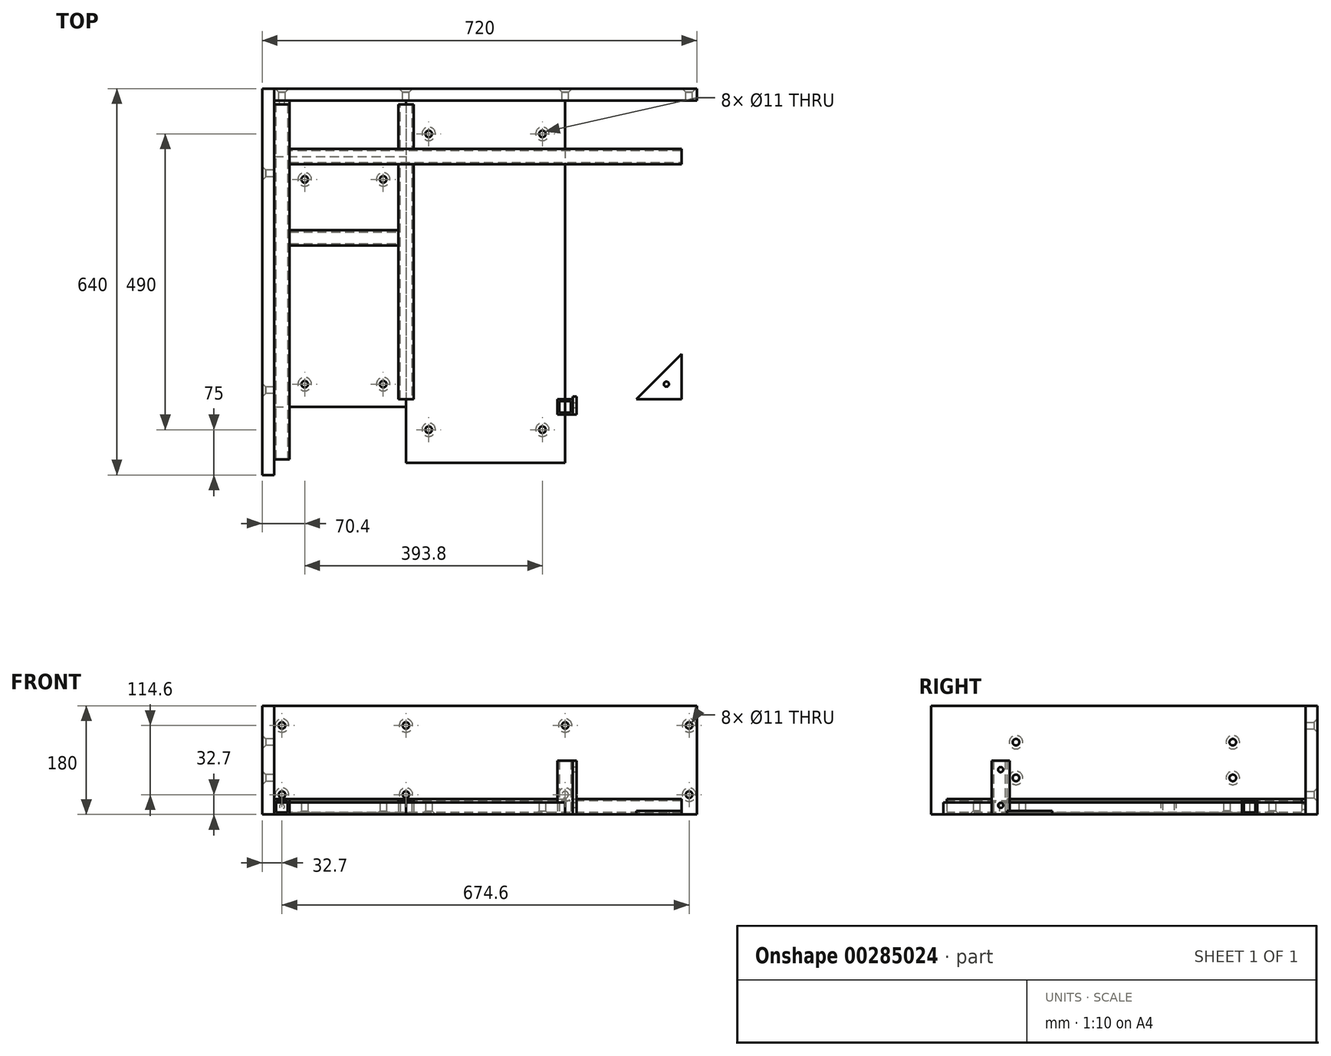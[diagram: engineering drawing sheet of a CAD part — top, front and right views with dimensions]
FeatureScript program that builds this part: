
annotation { "Feature Type Name" : "Feature", "Feature Type Description" : "" }
export const myFeature = defineFeature(function(context is Context, id is Id, definition is map)
    precondition{}
    {
        {
            assignVariable(context, id + "F0", {"name" : "plate", "anyValue" : 6});
        }
        {
            var Q0;
            Q0=qCreatedBy(makeId("Top.planeOp"),FACE);
            var sketch = newSketch(context, id + "F1", { "sketchPlane" : qUnion([Q0])});
            skLineSegment(sketch, "E0.bottom", {"start": v(350, -300) * mm, "end": v(-350, -300) * mm});
            skLineSegment(sketch, "E0.top", {"start": v(350, 300) * mm, "end": v(-350, 300) * mm});
            skLineSegment(sketch, "E0.left", {"start": v(350, -300) * mm, "end": v(350, 300) * mm});
            skLineSegment(sketch, "E0.right", {"start": v(-350, -300) * mm, "end": v(-350, 300) * mm});
            skPoint(sketch, "E0.middle", {"position": v(0, 0) * mm});
            skLineSegment(sketch, "E1", {"start": v(-324.6, 300) * mm, "end": v(-324.6, -300) * mm});
            skLineSegment(sketch, "E2", {"start": v(324.6, 300) * mm, "end": v(324.6, -300) * mm});
            skLineSegment(sketch, "E3", {"start": v(324.6, 220) * mm, "end": v(-324.6, 220) * mm});
            skLineSegment(sketch, "E4", {"start": v(-324.6, 194.6) * mm, "end": v(324.6, 194.6) * mm});
            skLineSegment(sketch, "E5", {"start": v(-119.2, 300) * mm, "end": v(-119.2, 220) * mm});
            skPoint(sketch, "E5.endSnap0", {"position": v(0, 220) * mm});
            skLineSegment(sketch, "E6", {"start": v(-144.6, 220) * mm, "end": v(-144.6, 300) * mm});
            skLineSegment(sketch, "E7.MirrorCS", {"start": v(119.2, 300) * mm, "end": v(119.2, 220) * mm});
            skLineSegment(sketch, "E8.MirrorCS", {"start": v(144.6, 220) * mm, "end": v(144.6, 300) * mm});
            skLineSegment(sketch, "E9", {"start": v(-350, 294) * mm, "end": v(350, 294) * mm});
            skLineSegment(sketch, "E10.MirrorCS", {"start": v(-324.6, -194.6) * mm, "end": v(324.6, -194.6) * mm});
            skLineSegment(sketch, "E11.MirrorCS", {"start": v(324.6, -220) * mm, "end": v(-324.6, -220) * mm});
            skLineSegment(sketch, "E12.MirrorCS", {"start": v(144.6, -220) * mm, "end": v(144.6, -300) * mm});
            skLineSegment(sketch, "E13.MirrorCS", {"start": v(119.2, -300) * mm, "end": v(119.2, -220) * mm});
            skLineSegment(sketch, "E14.MirrorCS", {"start": v(-119.2, -300) * mm, "end": v(-119.2, -220) * mm});
            skLineSegment(sketch, "E15.MirrorCS", {"start": v(-144.6, -220) * mm, "end": v(-144.6, -300) * mm});
            skLineSegment(sketch, "E16.MirrorCS", {"start": v(-350, -294) * mm, "end": v(350, -294) * mm});
            skLineSegment(sketch, "E17", {"start": v(-144.6, -194.6) * mm, "end": v(-144.6, 194.6) * mm});
            skLineSegment(sketch, "E18", {"start": v(-119.2, 194.6) * mm, "end": v(-119.2, -194.6) * mm});
            skLineSegment(sketch, "E19.MirrorCS", {"start": v(119.2, 194.6) * mm, "end": v(119.2, -194.6) * mm});
            skLineSegment(sketch, "E20.MirrorCS", {"start": v(144.6, -194.6) * mm, "end": v(144.6, 194.6) * mm});
            skLineSegment(sketch, "E21", {"start": v(-324.6, 60) * mm, "end": v(-144.6, 60) * mm});
            skLineSegment(sketch, "E22", {"start": v(-324.6, -60) * mm, "end": v(-144.6, -60) * mm});
            skLineSegment(sketch, "E23", {"start": v(-324.6, -85.4) * mm, "end": v(-144.6, -85.4) * mm});
            skLineSegment(sketch, "E24", {"start": v(-324.6, 85.4) * mm, "end": v(-144.6, 85.4) * mm});
            skSolve(sketch);
        }
        {
            var Q0;
            {var subQ3=sQuery(id+"F1.wireOp",EDGE,"E9");var subQ6=sQuery(id+"F1.wireOp",EDGE,"E0.right");var subQ7=makeQuery(id+"F1.imprint","INTERSECT",VERTEX,{"derivedFrom":[subQ6,subQ3]});Q0=makeQuery(id+"F1.imprint","IMPRINT",FACE,{"disambiguationData":[TD([[makeQuery(id+"F1.imprint","IMPRINT",EDGE,{"disambiguationData":[TD([[subQ7,1.0]])],"derivedFrom":subQ6}),-1.0]])]});}
            extrude(context, id + "F2", {"entities" : qUnion([Q0]), "depth" : 25.4 * mm});
        }
        {
            var Q0;
            {var subQ5=sQuery(id+"F1.wireOp",EDGE,"E4");Q0=makeQuery(id+"F1.imprint","IMPRINT",FACE,{"disambiguationData":[TD([[makeQuery(id+"F1.imprint","IMPRINT",EDGE,{"derivedFrom":subQ5}),1.0]])]});}
            extrude(context, id + "F3", {"entities" : qUnion([Q0]), "depth" : 25.4 * mm});
        }
        {
            var Q0;
            {var subQ0=sQuery(id+"F1.wireOp",EDGE,"E5");var subQ1=sQuery(id+"F1.wireOp",EDGE,"E3");var subQ2=makeQuery(id+"F1.imprint","INTERSECT",VERTEX,{"derivedFrom":[subQ1,subQ0]});Q0=makeQuery(id+"F1.imprint","IMPRINT",FACE,{"disambiguationData":[TD([[makeQuery(id+"F1.imprint","IMPRINT",EDGE,{"disambiguationData":[TD([[subQ2,-1.0]])],"derivedFrom":subQ1}),-1.0]])]});}
            extrude(context, id + "F4", {"entities" : qUnion([Q0]), "depth" : 25.4 * mm});
        }
        {
            var Q0;
            {var subQ0=sQuery(id+"F1.wireOp",EDGE,"E17");Q0=makeQuery(id+"F1.imprint","IMPRINT",FACE,{"disambiguationData":[TD([[makeQuery(id+"F1.imprint","IMPRINT",EDGE,{"derivedFrom":subQ0}),-1.0]])]});}
            extrude(context, id + "F5", {"entities" : qUnion([Q0]), "depth" : 25.4 * mm});
        }
        {
            var Q0;
            Q0=makeQuery(id+"F2.opExtrude","SWEPT_FACE",FACE,{"disambiguationData":[OSD([sQuery(id+"F1.wireOp",EDGE,"E9")])]});
            var Q1;
            Q1=makeQuery(id+"F2.opExtrude","SWEPT_FACE",FACE,{"disambiguationData":[OSD([sQuery(id+"F1.wireOp",EDGE,"E16.MirrorCS")])]});
            shell(context, id + "F6", {"entities" : qUnion([Q0, Q1]), "thickness" : 3.17 * mm});
        }
        {
            var Q0;
            Q0=makeQuery(id+"F3.opExtrude","SWEPT_FACE",FACE,{"disambiguationData":[OSD([sQuery(id+"F1.wireOp",EDGE,"E1")])]});
            var Q1;
            Q1=makeQuery(id+"F3.opExtrude","SWEPT_FACE",FACE,{"disambiguationData":[OSD([sQuery(id+"F1.wireOp",EDGE,"E2")])]});
            shell(context, id + "F7", {"entities" : qUnion([Q0, Q1]), "thickness" : 3.17 * mm});
        }
        {
            var Q0;
            Q0=makeQuery(id+"F4.opExtrude","SWEPT_FACE",FACE,{"disambiguationData":[OSD([sQuery(id+"F1.wireOp",EDGE,"E9")])]});
            var Q1;
            Q1=makeQuery(id+"F4.opExtrude","SWEPT_FACE",FACE,{"disambiguationData":[OSD([sQuery(id+"F1.wireOp",EDGE,"E3")])]});
            shell(context, id + "F8", {"entities" : qUnion([Q0, Q1]), "thickness" : 3.17 * mm});
        }
        {
            var Q0;
            Q0=makeQuery(id+"F5.opExtrude","SWEPT_FACE",FACE,{"disambiguationData":[OSD([sQuery(id+"F1.wireOp",EDGE,"E10.MirrorCS")])]});
            var Q1;
            Q1=makeQuery(id+"F5.opExtrude","SWEPT_FACE",FACE,{"disambiguationData":[OSD([sQuery(id+"F1.wireOp",EDGE,"E4")])]});
            shell(context, id + "F9", {"entities" : qUnion([Q0, Q1]), "thickness" : 3.17 * mm});
        }
        {
            var Q0;
            {var subQ0=sQuery(id+"F1.wireOp",EDGE,"E0.right");var subQ1=sQuery(id+"F1.wireOp",EDGE,"E0.top");var subQ2=makeQuery(id+"F1.imprint","INTERSECT",VERTEX,{"derivedFrom":[subQ1,subQ0]});Q0=makeQuery(id+"F1.imprint","IMPRINT",FACE,{"disambiguationData":[TD([[makeQuery(id+"F1.imprint","IMPRINT",EDGE,{"disambiguationData":[TD([[subQ2,1.0]])],"derivedFrom":subQ1}),1.0]])]});}
            extrude(context, id + "F10", {"entities" : qUnion([Q0]), "depth" : 25.4 * mm});
        }
        {
            var Q0;
            Q0=makeQuery(id+"F10.opExtrude","SWEPT_FACE",FACE,{"disambiguationData":[OSD([sQuery(id+"F1.wireOp",EDGE,"E0.top")])]});
            var sketch = newSketch(context, id + "F11", { "sketchPlane" : qUnion([Q0])});
            skLineSegment(sketch, "E25", {"start": v(324.6, 25.4) * mm, "end": v(350, 0) * mm});
            skPoint(sketch, "E26", {"position": v(337.3, 12.7) * mm});
            skSolve(sketch);
        }
        {
            var Q0;
            Q0=sQuery(id+"F11.wireOp",VERTEX,"E26");
            var Q1;
            Q1=makeQuery(id+"F10.opExtrude","SWEPT_BODY",BODY,{"disambiguationData":[OSD([sQuery(id+"F1.wireOp",EDGE,"E0.top"),sQuery(id+"F1.wireOp",EDGE,"E0.right"),sQuery(id+"F1.wireOp",EDGE,"E1"),sQuery(id+"F1.wireOp",EDGE,"E9")])]});
            hole(context, id + "F12", {"style" : HoleStyle.SIMPLE, "endStyle" : HoleEndStyle.THROUGH, "standardTappedOrClearance" : lookupTablePath({ "standard" : "ISO", "engagement" : "75%", "pitch" : "1.5 mm", "size" : "M10", "type" : "Tapped" }), "standardBlindInLast" : lookupTablePath({ "standard" : "ISO", "engagement" : "75%", "pitch" : "1.5 mm", "size" : "M10", "type" : "Tapped" }), "holeDiameter" : 8.5 * mm, "showTappedDepth" : true, "tappedDepth" : 12 * mm, "tapClearance" : 3, "locations" : qUnion([Q0]), "scope" : qUnion([Q1]), "majorDiameter" : 10 * mm});
        }
        {
            var Q0;
            Q0=qCreatedBy(makeId("Top.planeOp"),FACE);
            var sketch = newSketch(context, id + "F13", { "sketchPlane" : qUnion([Q0])});
            skLineSegment(sketch, "E27", {"start": v(249.6, -194.6) * mm, "end": v(324.6, -119.6) * mm});
            skLineSegment(sketch, "E28", {"start": v(324.6, -119.6) * mm, "end": v(324.6, -194.6) * mm});
            skLineSegment(sketch, "E29", {"start": v(324.6, -194.6) * mm, "end": v(249.6, -194.6) * mm});
            skPoint(sketch, "E30", {"position": v(299.6, -169.6) * mm});
            skSolve(sketch);
        }
        {
            var Q0;
            Q0=qSketchRegion(id+"F13",true);
            extrude(context, id + "F14", {"entities" : qUnion([Q0]), "depth" : (getVariable(context, 'plate')) * mm});
        }
        {
            var Q0;
            Q0=sQuery(id+"F13.wireOp",VERTEX,"E30");
            var Q1;
            Q1=makeQuery(id+"F14.opExtrude","SWEPT_BODY",BODY,{"disambiguationData":[OSD([sQuery(id+"F13.wireOp",EDGE,"E27"),sQuery(id+"F13.wireOp",EDGE,"E28"),sQuery(id+"F13.wireOp",EDGE,"E29")])]});
            hole(context, id + "F15", {"style" : HoleStyle.SIMPLE, "endStyle" : HoleEndStyle.THROUGH, "oppositeDirection" : true, "standardTappedOrClearance" : lookupTablePath({ "standard" : "ISO", "engagement" : "75%", "pitch" : "1.5 mm", "size" : "M10", "type" : "Tapped" }), "standardBlindInLast" : lookupTablePath({ "standard" : "ISO", "engagement" : "75%", "pitch" : "1.5 mm", "size" : "M10", "type" : "Tapped" }), "holeDiameter" : 8.5 * mm, "showTappedDepth" : true, "tappedDepth" : 12 * mm, "tapClearance" : 3, "locations" : qUnion([Q0]), "scope" : qUnion([Q1]), "majorDiameter" : 10 * mm});
        }
        {
            var Q0;
            {var subQ0=sQuery(id+"F1.wireOp",EDGE,"E18");Q0=makeQuery(id+"F1.imprint","IMPRINT",FACE,{"disambiguationData":[TD([[makeQuery(id+"F1.imprint","IMPRINT",EDGE,{"derivedFrom":subQ0}),1.0]])]});}
            var sketch = newSketch(context, id + "F16", { "sketchPlane" : qUnion([Q0])});
            skLineSegment(sketch, "E31.bottom", {"start": v(-350, 300) * mm, "end": v(350, 300) * mm});
            skLineSegment(sketch, "E31.top", {"start": v(-350, 320) * mm, "end": v(350, 320) * mm});
            skLineSegment(sketch, "E31.left", {"start": v(-350, 300) * mm, "end": v(-350, 320) * mm});
            skLineSegment(sketch, "E31.right", {"start": v(350, 300) * mm, "end": v(350, 320) * mm});
            skSolve(sketch);
        }
        {
            var Q0;
            Q0=makeQuery(id+"F16.imprint","IMPRINT",FACE,{"disambiguationData":[TD([[makeQuery(id+"F16.imprint","IMPRINT",EDGE,{"derivedFrom":sQuery(id+"F16.wireOp",EDGE,"E31.bottom")}),1.0]])]});
            extrude(context, id + "F17", {"entities" : qUnion([Q0]), "depth" : 180 * mm});
        }
        {
            var Q0;
            Q0=makeQuery(id+"F17.opExtrude","SWEPT_FACE",FACE,{"disambiguationData":[OSD([sQuery(id+"F16.wireOp",EDGE,"E31.top")])]});
            var sketch = newSketch(context, id + "F18", { "sketchPlane" : qUnion([Q0])});
            skPoint(sketch, "E32", {"position": v(-337.3, 32.7) * mm});
            skPoint(sketch, "E33", {"position": v(-131.9, 32.7) * mm});
            skPoint(sketch, "E34.MirrorP", {"position": v(131.9, 32.7) * mm});
            skPoint(sketch, "E35.MirrorP", {"position": v(337.3, 32.7) * mm});
            skLineSegment(sketch, "E36", {"start": v(-350, 90) * mm, "end": v(350, 90) * mm});
            skPoint(sketch, "E37.MirrorP", {"position": v(-131.9, 147.3) * mm});
            skPoint(sketch, "E38.MirrorP", {"position": v(-337.3, 147.3) * mm});
            skPoint(sketch, "E39.MirrorP", {"position": v(131.9, 147.3) * mm});
            skPoint(sketch, "E40.MirrorP", {"position": v(337.3, 147.3) * mm});
            skSolve(sketch);
        }
        {
            var Q0;
            Q0=sQuery(id+"F18.wireOp",VERTEX,"E37.MirrorP");
            var Q1;
            Q1=sQuery(id+"F18.wireOp",VERTEX,"E33");
            var Q2;
            Q2=sQuery(id+"F18.wireOp",VERTEX,"E38.MirrorP");
            var Q3;
            Q3=sQuery(id+"F18.wireOp",VERTEX,"E32");
            var Q4;
            Q4=sQuery(id+"F18.wireOp",VERTEX,"E39.MirrorP");
            var Q5;
            Q5=sQuery(id+"F18.wireOp",VERTEX,"E34.MirrorP");
            var Q6;
            Q6=sQuery(id+"F18.wireOp",VERTEX,"E40.MirrorP");
            var Q7;
            Q7=sQuery(id+"F18.wireOp",VERTEX,"E35.MirrorP");
            var Q8;
            Q8=makeQuery(id+"F17.opExtrude","SWEPT_BODY",BODY,{"disambiguationData":[OSD([sQuery(id+"F16.wireOp",EDGE,"E31.bottom"),sQuery(id+"F16.wireOp",EDGE,"E31.top"),sQuery(id+"F16.wireOp",EDGE,"E31.left"),sQuery(id+"F16.wireOp",EDGE,"E31.right")])]});
            hole(context, id + "F19", {"style" : HoleStyle.C_SINK, "endStyle" : HoleEndStyle.THROUGH, "standardTappedOrClearance" : lookupTablePath({ "standard" : "ISO", "fit" : "Normal", "size" : "M10", "type" : "Clearance" }), "standardBlindInLast" : lookupTablePath({ "fit" : "Standard", "standard" : "ISO", "size" : "M10", "type" : "Clearance" }), "holeDiameter" : 11 * mm, "cSinkDiameter" : 22.4 * mm, "cSinkAngle" : 90 * degree, "tappedDepth" : 12 * mm, "tapClearance" : 3, "locations" : qUnion([Q0, Q1, Q2, Q3, Q4, Q5, Q6, Q7]), "scope" : qUnion([Q8])});
        }
        {
            var Q0;
            Q0=qCreatedBy(makeId("Top.planeOp"),FACE);
            var sketch = newSketch(context, id + "F20", { "sketchPlane" : qUnion([Q0])});
            skLineSegment(sketch, "E41.bottom", {"start": v(-370, -320) * mm, "end": v(-350, -320) * mm});
            skLineSegment(sketch, "E41.top", {"start": v(-370, 320) * mm, "end": v(-350, 320) * mm});
            skLineSegment(sketch, "E41.left", {"start": v(-370, -320) * mm, "end": v(-370, 320) * mm});
            skLineSegment(sketch, "E41.right", {"start": v(-350, -320) * mm, "end": v(-350, 320) * mm});
            skSolve(sketch);
        }
        {
            var Q0;
            Q0=qSketchRegion(id+"F20",true);
            extrude(context, id + "F21", {"entities" : qUnion([Q0]), "depth" : 180 * mm});
        }
        {
            var Q0;
            Q0=qCreatedBy(makeId("Top.planeOp"),FACE);
            var sketch = newSketch(context, id + "F22", { "sketchPlane" : qUnion([Q0])});
            skLineSegment(sketch, "E42.bottom", {"start": v(-350, -300) * mm, "end": v(350, -300) * mm});
            skLineSegment(sketch, "E42.top", {"start": v(-350, 300) * mm, "end": v(350, 300) * mm});
            skLineSegment(sketch, "E42.left", {"start": v(-350, -300) * mm, "end": v(-350, 300) * mm});
            skLineSegment(sketch, "E42.right", {"start": v(350, -300) * mm, "end": v(350, 300) * mm});
            skLineSegment(sketch, "E43", {"start": v(-350, 207.3) * mm, "end": v(350, 207.3) * mm});
            skLineSegment(sketch, "E44.MirrorCS", {"start": v(-350, -207.3) * mm, "end": v(350, -207.3) * mm});
            skLineSegment(sketch, "E45", {"start": v(-131.9, 300) * mm, "end": v(-131.9, -300) * mm});
            skLineSegment(sketch, "E46.MirrorCS", {"start": v(131.9, 300) * mm, "end": v(131.9, -300) * mm});
            skPoint(sketch, "E47", {"position": v(-299.6, 169.6) * mm});
            skPoint(sketch, "E48", {"position": v(-299.6, -169.6) * mm});
            skPoint(sketch, "E49", {"position": v(-169.6, -169.6) * mm});
            skPoint(sketch, "E50", {"position": v(-169.6, 169.6) * mm});
            skPoint(sketch, "E51", {"position": v(169.6, -169.6) * mm});
            skPoint(sketch, "E52", {"position": v(169.6, 169.6) * mm});
            skPoint(sketch, "E53", {"position": v(299.6, 169.6) * mm});
            skPoint(sketch, "E54", {"position": v(299.6, -169.6) * mm});
            skPoint(sketch, "E55", {"position": v(-94.2, 245) * mm});
            skPoint(sketch, "E56.MirrorP", {"position": v(94.2, 245) * mm});
            skPoint(sketch, "E57.MirrorP", {"position": v(94.2, -245) * mm});
            skPoint(sketch, "E58.MirrorP", {"position": v(-94.2, -245) * mm});
            skSolve(sketch);
        }
        {
            var Q0;
            {var subQ0=sQuery(id+"F22.wireOp",EDGE,"E43");var subQ1=sQuery(id+"F22.wireOp",EDGE,"E42.left");var subQ2=makeQuery(id+"F22.imprint","INTERSECT",VERTEX,{"derivedFrom":[subQ1,subQ0]});Q0=makeQuery(id+"F22.imprint","IMPRINT",FACE,{"disambiguationData":[TD([[makeQuery(id+"F22.imprint","IMPRINT",EDGE,{"disambiguationData":[TD([[subQ2,1.0]])],"derivedFrom":subQ1}),-1.0]])]});}
            extrude(context, id + "F23", {"entities" : qUnion([Q0]), "depth" : 20 * mm});
        }
        {
            var Q0;
            {var subQ0=sQuery(id+"F22.wireOp",EDGE,"E45");var subQ1=sQuery(id+"F22.wireOp",EDGE,"E42.top");var subQ2=makeQuery(id+"F22.imprint","INTERSECT",VERTEX,{"derivedFrom":[subQ1,subQ0]});Q0=makeQuery(id+"F22.imprint","IMPRINT",FACE,{"disambiguationData":[TD([[makeQuery(id+"F22.imprint","IMPRINT",EDGE,{"disambiguationData":[TD([[subQ2,-1.0]])],"derivedFrom":subQ1}),-1.0]])]});}
            var Q1;
            {var subQ0=sQuery(id+"F22.wireOp",EDGE,"E45");var subQ1=sQuery(id+"F22.wireOp",EDGE,"E43");var subQ2=makeQuery(id+"F22.imprint","INTERSECT",VERTEX,{"derivedFrom":[subQ1,subQ0]});Q1=makeQuery(id+"F22.imprint","IMPRINT",FACE,{"disambiguationData":[TD([[makeQuery(id+"F22.imprint","IMPRINT",EDGE,{"disambiguationData":[TD([[subQ2,-1.0]])],"derivedFrom":subQ1}),-1.0]])]});}
            var Q2;
            {var subQ0=sQuery(id+"F22.wireOp",EDGE,"E45");var subQ1=sQuery(id+"F22.wireOp",EDGE,"E42.bottom");var subQ2=makeQuery(id+"F22.imprint","INTERSECT",VERTEX,{"derivedFrom":[subQ1,subQ0]});Q2=makeQuery(id+"F22.imprint","IMPRINT",FACE,{"disambiguationData":[TD([[makeQuery(id+"F22.imprint","IMPRINT",EDGE,{"disambiguationData":[TD([[subQ2,-1.0]])],"derivedFrom":subQ1}),1.0]])]});}
            extrude(context, id + "F24", {"entities" : qUnion([Q0, Q1, Q2]), "depth" : 20 * mm});
        }
        {
            var Q0;
            Q0=sQuery(id+"F22.wireOp",VERTEX,"E47");
            var Q1;
            Q1=sQuery(id+"F22.wireOp",VERTEX,"E50");
            var Q2;
            Q2=sQuery(id+"F22.wireOp",VERTEX,"E49");
            var Q3;
            Q3=sQuery(id+"F22.wireOp",VERTEX,"E48");
            var Q4;
            Q4=makeQuery(id+"F23.opExtrude","SWEPT_BODY",BODY,{"disambiguationData":[OSD([sQuery(id+"F22.wireOp",EDGE,"E42.left"),sQuery(id+"F22.wireOp",EDGE,"E43"),sQuery(id+"F22.wireOp",EDGE,"E44.MirrorCS"),sQuery(id+"F22.wireOp",EDGE,"E45")])]});
            hole(context, id + "F25", {"style" : HoleStyle.C_SINK, "endStyle" : HoleEndStyle.THROUGH, "oppositeDirection" : true, "standardTappedOrClearance" : lookupTablePath({ "standard" : "ISO", "fit" : "Normal", "size" : "M10", "type" : "Clearance" }), "standardBlindInLast" : lookupTablePath({ "fit" : "Standard", "standard" : "ISO", "size" : "M10", "type" : "Clearance" }), "holeDiameter" : 11 * mm, "cSinkDiameter" : 22.4 * mm, "cSinkAngle" : 90 * degree, "tappedDepth" : 12 * mm, "tapClearance" : 3, "locations" : qUnion([Q0, Q1, Q2, Q3]), "scope" : qUnion([Q4])});
        }
        {
            var Q0;
            Q0=sQuery(id+"F22.wireOp",VERTEX,"E55");
            var Q1;
            Q1=sQuery(id+"F22.wireOp",VERTEX,"E56.MirrorP");
            var Q2;
            Q2=sQuery(id+"F22.wireOp",VERTEX,"E58.MirrorP");
            var Q3;
            Q3=sQuery(id+"F22.wireOp",VERTEX,"E57.MirrorP");
            var Q4;
            Q4=makeQuery(id+"F24.opExtrude","SWEPT_BODY",BODY,{"disambiguationData":[OSD([sQuery(id+"F22.wireOp",EDGE,"E42.bottom"),sQuery(id+"F22.wireOp",EDGE,"E42.top"),sQuery(id+"F22.wireOp",EDGE,"E45"),sQuery(id+"F22.wireOp",EDGE,"E46.MirrorCS")])]});
            hole(context, id + "F26", {"style" : HoleStyle.C_SINK, "endStyle" : HoleEndStyle.THROUGH, "oppositeDirection" : true, "standardTappedOrClearance" : lookupTablePath({ "standard" : "ISO", "fit" : "Normal", "size" : "M10", "type" : "Clearance" }), "standardBlindInLast" : lookupTablePath({ "fit" : "Standard", "standard" : "ISO", "size" : "M10", "type" : "Clearance" }), "holeDiameter" : 11 * mm, "cSinkDiameter" : 22.4 * mm, "cSinkAngle" : 90 * degree, "tappedDepth" : 12 * mm, "tapClearance" : 3, "locations" : qUnion([Q0, Q1, Q2, Q3]), "scope" : qUnion([Q4])});
        }
        {
            var Q0;
            Q0=qCreatedBy(makeId("Top.planeOp"),FACE);
            var sketch = newSketch(context, id + "F27", { "sketchPlane" : qUnion([Q0])});
            skLineSegment(sketch, "E59.bottom", {"start": v(144.6, -220) * mm, "end": v(119.2, -220) * mm});
            skLineSegment(sketch, "E59.top", {"start": v(144.6, -194.6) * mm, "end": v(119.2, -194.6) * mm});
            skLineSegment(sketch, "E59.left", {"start": v(144.6, -220) * mm, "end": v(144.6, -194.6) * mm});
            skLineSegment(sketch, "E59.right", {"start": v(119.2, -220) * mm, "end": v(119.2, -194.6) * mm});
            skSolve(sketch);
        }
        {
            var Q0;
            Q0=qSketchRegion(id+"F27",true);
            extrude(context, id + "F28", {"entities" : qUnion([Q0]), "depth" : (140 - 50.8) * mm});
        }
        {
            var Q0;
            Q0=makeQuery(id+"F28.opExtrude","CAP_FACE",FACE,{"disambiguationData":[OSD([sQuery(id+"F27.wireOp",EDGE,"E59.bottom"),sQuery(id+"F27.wireOp",EDGE,"E59.top"),sQuery(id+"F27.wireOp",EDGE,"E59.left"),sQuery(id+"F27.wireOp",EDGE,"E59.right")])],"isStart":false});
            var Q1;
            Q1=makeQuery(id+"F28.opExtrude","CAP_FACE",FACE,{"disambiguationData":[OSD([sQuery(id+"F27.wireOp",EDGE,"E59.bottom"),sQuery(id+"F27.wireOp",EDGE,"E59.top"),sQuery(id+"F27.wireOp",EDGE,"E59.left"),sQuery(id+"F27.wireOp",EDGE,"E59.right")])],"isStart":true});
            shell(context, id + "F29", {"entities" : qUnion([Q0, Q1]), "thickness" : 3.17 * mm});
        }
        {
            var Q0;
            Q0=makeQuery(id+"F28.opExtrude","SWEPT_FACE",FACE,{"disambiguationData":[OSD([sQuery(id+"F27.wireOp",EDGE,"E59.left")])]});
            var sketch = newSketch(context, id + "F30", { "sketchPlane" : qUnion([Q0])});
            skLineSegment(sketch, "E60.bottom", {"start": v(-220, 89.2) * mm, "end": v(-190, 89.2) * mm});
            skLineSegment(sketch, "E60.top", {"start": v(-220, 0) * mm, "end": v(-190, 0) * mm});
            skLineSegment(sketch, "E60.left", {"start": v(-220, 89.2) * mm, "end": v(-220, 0) * mm});
            skLineSegment(sketch, "E60.right", {"start": v(-190, 89.2) * mm, "end": v(-190, 0) * mm});
            skPoint(sketch, "E61", {"position": v(-205, 74.2) * mm});
            skPoint(sketch, "E61.positionSnap0", {"position": v(-205, 89.2) * mm});
            skPoint(sketch, "E62", {"position": v(-205, 15) * mm});
            skSolve(sketch);
        }
        {
            var Q0;
            Q0=makeQuery(id+"F30.imprint","IMPRINT",FACE,{"disambiguationData":[TD([[makeQuery(id+"F30.imprint","IMPRINT",EDGE,{"derivedFrom":sQuery(id+"F30.wireOp",EDGE,"E60.bottom")}),-1.0]])]});
            extrude(context, id + "F31", {"entities" : qUnion([Q0]), "depth" : (getVariable(context, 'plate')) * mm});
        }
        {
            var Q0;
            Q0=sQuery(id+"F30.wireOp",VERTEX,"E61");
            var Q1;
            Q1=sQuery(id+"F30.wireOp",VERTEX,"E62");
            var Q2;
            Q2=makeQuery(id+"F31.opExtrude","SWEPT_BODY",BODY,{"disambiguationData":[OSD([sQuery(id+"F30.wireOp",EDGE,"E60.bottom"),sQuery(id+"F30.wireOp",EDGE,"E60.top"),sQuery(id+"F30.wireOp",EDGE,"E60.left"),sQuery(id+"F30.wireOp",EDGE,"E60.right")])]});
            hole(context, id + "F32", {"style" : HoleStyle.SIMPLE, "endStyle" : HoleEndStyle.THROUGH, "oppositeDirection" : true, "standardTappedOrClearance" : lookupTablePath({ "standard" : "ISO", "engagement" : "75%", "pitch" : "1.5 mm", "size" : "M10", "type" : "Tapped" }), "standardBlindInLast" : lookupTablePath({ "standard" : "ISO", "engagement" : "75%", "pitch" : "1.5 mm", "size" : "M10", "type" : "Tapped" }), "holeDiameter" : 8.5 * mm, "showTappedDepth" : true, "tappedDepth" : 12 * mm, "tapClearance" : 3, "locations" : qUnion([Q0, Q1]), "scope" : qUnion([Q2]), "majorDiameter" : 10 * mm});
        }
        {
            var Q0;
            Q0=makeQuery(id+"F21.opExtrude","SWEPT_FACE",FACE,{"disambiguationData":[OSD([sQuery(id+"F20.wireOp",EDGE,"E41.left")])]});
            var sketch = newSketch(context, id + "F33", { "sketchPlane" : qUnion([Q0])});
            skLineSegment(sketch, "E63.bottom", {"start": v(-179.6, 119.6) * mm, "end": v(179.6, 119.6) * mm});
            skLineSegment(sketch, "E63.top", {"start": v(-179.6, 60.4) * mm, "end": v(179.6, 60.4) * mm});
            skLineSegment(sketch, "E63.left", {"start": v(-179.6, 119.6) * mm, "end": v(-179.6, 60.4) * mm});
            skLineSegment(sketch, "E63.right", {"start": v(179.6, 119.6) * mm, "end": v(179.6, 60.4) * mm});
            skLineSegment(sketch, "E64", {"start": v(0, 119.6) * mm, "end": v(0, 180) * mm});
            skLineSegment(sketch, "E65", {"start": v(-320, 90) * mm, "end": v(-179.6, 90) * mm});
            skSolve(sketch);
        }
        {
            var Q0;
            Q0=sQuery(id+"F33.wireOp",VERTEX,"E63.left.start");
            var Q1;
            Q1=sQuery(id+"F33.wireOp",VERTEX,"E63.left.end");
            var Q2;
            Q2=sQuery(id+"F33.wireOp",VERTEX,"E63.right.start");
            var Q3;
            Q3=sQuery(id+"F33.wireOp",VERTEX,"E63.right.end");
            var Q4;
            Q4=makeQuery(id+"F21.opExtrude","SWEPT_BODY",BODY,{"disambiguationData":[OSD([sQuery(id+"F20.wireOp",EDGE,"E41.bottom"),sQuery(id+"F20.wireOp",EDGE,"E41.top"),sQuery(id+"F20.wireOp",EDGE,"E41.left"),sQuery(id+"F20.wireOp",EDGE,"E41.right")])]});
            hole(context, id + "F34", {"style" : HoleStyle.C_SINK, "endStyle" : HoleEndStyle.THROUGH, "standardTappedOrClearance" : lookupTablePath({ "standard" : "ISO", "fit" : "Normal", "size" : "M10", "type" : "Clearance" }), "standardBlindInLast" : lookupTablePath({ "fit" : "Standard", "standard" : "ISO", "size" : "M10", "type" : "Clearance" }), "holeDiameter" : 11 * mm, "cSinkDiameter" : 22.4 * mm, "cSinkAngle" : 90 * degree, "tappedDepth" : 12 * mm, "tapClearance" : 3, "locations" : qUnion([Q0, Q1, Q2, Q3]), "scope" : qUnion([Q4])});
        }
        {
            var Q0;
            {var subQ0=sQuery(id+"F1.wireOp",EDGE,"E21");Q0=makeQuery(id+"F1.imprint","IMPRINT",FACE,{"disambiguationData":[TD([[makeQuery(id+"F1.imprint","IMPRINT",EDGE,{"derivedFrom":subQ0}),1.0]])]});}
            extrude(context, id + "F35", {"entities" : qUnion([Q0]), "depth" : 25.4 * mm});
        }
        {
            var Q0;
            Q0=makeQuery(id+"F35.opExtrude","SWEPT_FACE",FACE,{"disambiguationData":[OSD([sQuery(id+"F1.wireOp",EDGE,"E1")])]});
            var Q1;
            Q1=makeQuery(id+"F35.opExtrude","SWEPT_FACE",FACE,{"disambiguationData":[OSD([sQuery(id+"F1.wireOp",EDGE,"E17")])]});
            shell(context, id + "F36", {"entities" : qUnion([Q0, Q1]), "thickness" : 3.17 * mm});
        }
    });
